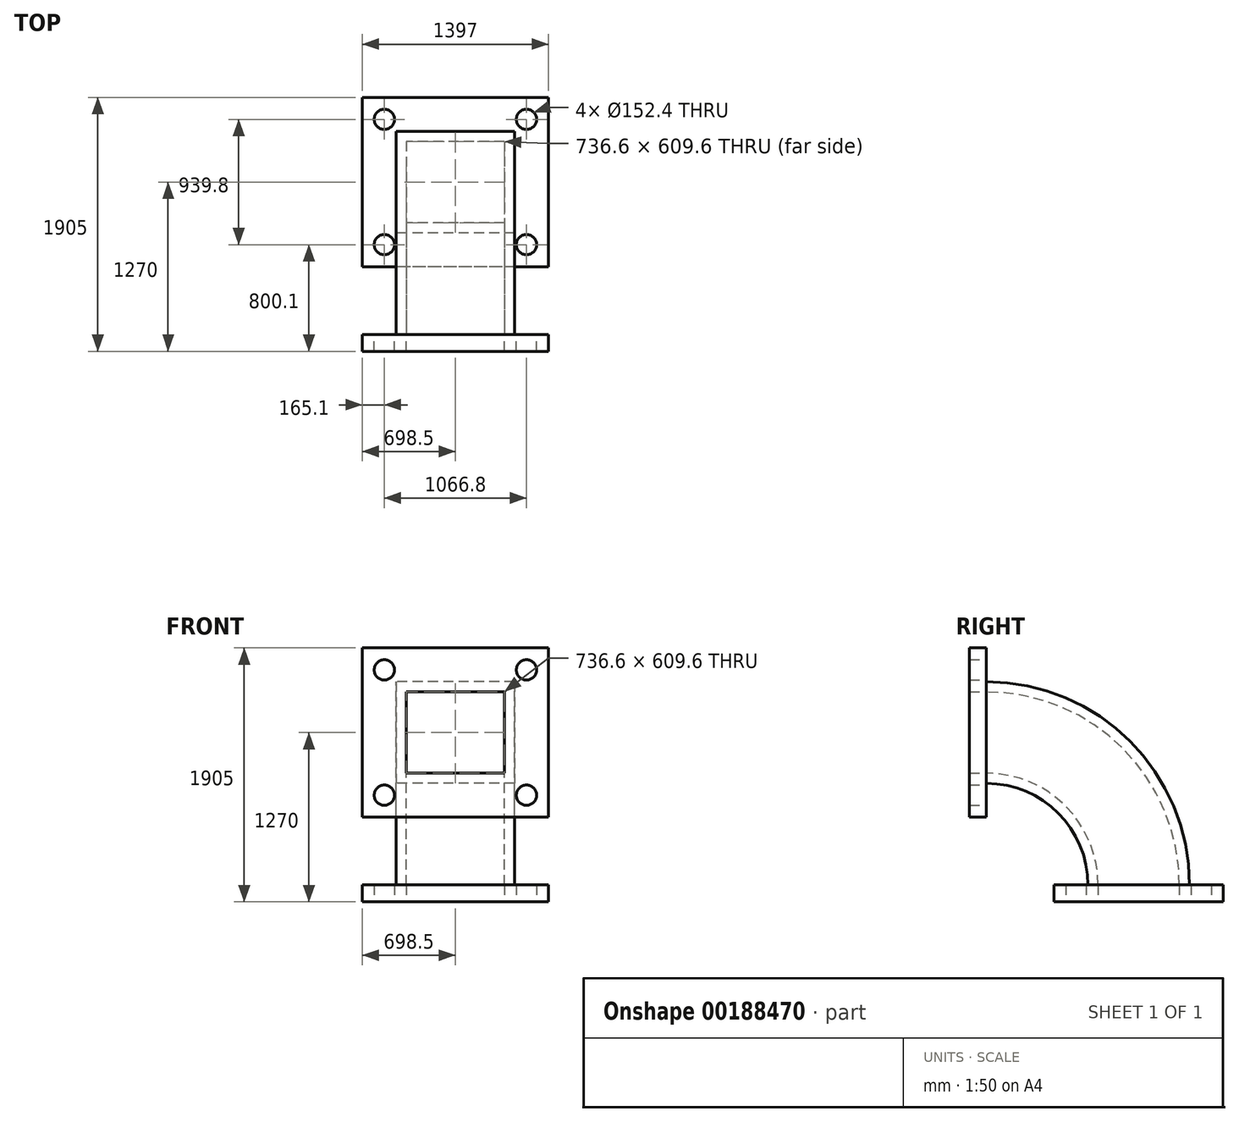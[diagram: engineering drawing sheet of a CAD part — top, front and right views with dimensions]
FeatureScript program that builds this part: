
annotation { "Feature Type Name" : "Feature", "Feature Type Description" : "" }
export const myFeature = defineFeature(function(context is Context, id is Id, definition is map)
    precondition{}
    {
        {
            var Q0;
            Q0=qCreatedBy(makeId("Front.planeOp"),FACE);
            var sketch = newSketch(context, id + "F0", { "sketchPlane" : qUnion([Q0])});
            skLineSegment(sketch, "E0.bottom", {"start": v(698.5, 635) * mm, "end": v(-698.5, 635) * mm});
            skLineSegment(sketch, "E0.top", {"start": v(698.5, -635) * mm, "end": v(-698.5, -635) * mm});
            skLineSegment(sketch, "E0.left", {"start": v(698.5, 635) * mm, "end": v(698.5, -635) * mm});
            skLineSegment(sketch, "E0.right", {"start": v(-698.5, 635) * mm, "end": v(-698.5, -635) * mm});
            skPoint(sketch, "E0.middle", {"position": v(0, 0) * mm});
            skLineSegment(sketch, "E1.bottom", {"start": v(368.3, 304.8) * mm, "end": v(-368.3, 304.8) * mm});
            skLineSegment(sketch, "E1.top", {"start": v(368.3, -304.8) * mm, "end": v(-368.3, -304.8) * mm});
            skLineSegment(sketch, "E1.left", {"start": v(368.3, 304.8) * mm, "end": v(368.3, -304.8) * mm});
            skLineSegment(sketch, "E1.right", {"start": v(-368.3, 304.8) * mm, "end": v(-368.3, -304.8) * mm});
            skCircle(sketch, "E2", {"center": v(533.4, 469.9) * mm, "radius": 76.2 * mm});
            skPoint(sketch, "E3.startSnap0", {"position": v(-698.5, 0) * mm});
            skCircle(sketch, "E4.MirrorC", {"center": v(-533.4, 469.9) * mm, "radius": 76.2 * mm});
            skCircle(sketch, "E5.MirrorC", {"center": v(-533.4, -469.9) * mm, "radius": 76.2 * mm});
            skCircle(sketch, "E6.MirrorC", {"center": v(533.4, -469.9) * mm, "radius": 76.2 * mm});
            skSolve(sketch);
        }
        {
            var Q0;
            Q0=qCreatedBy(makeId("Right.planeOp"),FACE);
            var sketch = newSketch(context, id + "F1", { "sketchPlane" : qUnion([Q0])});
            skCircle(sketch, "E7", {"center": v(0, -1143) * mm, "radius": 838.2 * mm});
            skCircle(sketch, "E8", {"center": v(0, -1143) * mm, "radius": 762 * mm});
            skLineSegment(sketch, "E9", {"start": v(-678.7, -1143) * mm, "end": v(1388.13, -1143) * mm});
            skSolve(sketch);
        }
        {
            var Q0;
            Q0=makeQuery(id+"F0.imprint","IMPRINT",FACE,{"disambiguationData":[TD([[makeQuery(id+"F0.imprint","IMPRINT",EDGE,{"derivedFrom":sQuery(id+"F0.wireOp",EDGE,"E0.bottom")}),1.0]])]});
            extrude(context, id + "F2", {"entities" : qUnion([Q0]), "depth" : 127 * mm});
        }
        {
            var Q0;
            Q0=makeQuery(id+"F2.opExtrude","CAP_FACE",FACE,{"disambiguationData":[OSD([sQuery(id+"F0.wireOp",EDGE,"E0.bottom"),sQuery(id+"F0.wireOp",EDGE,"E0.top"),sQuery(id+"F0.wireOp",EDGE,"E0.left"),sQuery(id+"F0.wireOp",EDGE,"E0.right"),sQuery(id+"F0.wireOp",EDGE,"E1.bottom"),sQuery(id+"F0.wireOp",EDGE,"E1.top"),sQuery(id+"F0.wireOp",EDGE,"E1.left"),sQuery(id+"F0.wireOp",EDGE,"E1.right"),sQuery(id+"F0.wireOp",EDGE,"E2"),sQuery(id+"F0.wireOp",EDGE,"E4.MirrorC"),sQuery(id+"F0.wireOp",EDGE,"E5.MirrorC"),sQuery(id+"F0.wireOp",EDGE,"E6.MirrorC")])],"isStart":true});
            var sketch = newSketch(context, id + "F3", { "sketchPlane" : qUnion([Q0])});
            skLineSegment(sketch, "E10.bottom", {"start": v(-444.5, 381) * mm, "end": v(444.5, 381) * mm});
            skLineSegment(sketch, "E10.top", {"start": v(-444.5, -381) * mm, "end": v(444.5, -381) * mm});
            skLineSegment(sketch, "E10.left", {"start": v(-444.5, 381) * mm, "end": v(-444.5, -381) * mm});
            skLineSegment(sketch, "E10.right", {"start": v(444.5, 381) * mm, "end": v(444.5, -381) * mm});
            skPoint(sketch, "E10.middle", {"position": v(0, 0) * mm});
            skSolve(sketch);
        }
        {
            var Q0;
            Q0=qCreatedBy(makeId("Top.planeOp"),FACE);
            var Q1;
            Q1=sQuery(id+"F1.wireOp",VERTEX,"E8.center");
            cPlane(context, id + "F4", {"entities" : qUnion([Q0, Q1]), "cplaneType" : CPlaneType.PLANE_POINT, "offset" : 25.4 * mm, "width" : 152.4 * mm, "height" : 152.4 * mm});
        }
        {
            var Q0;
            Q0=qCreatedBy(id+"F4.planeOp",FACE);
            var sketch = newSketch(context, id + "F5", { "sketchPlane" : qUnion([Q0])});
            skLineSegment(sketch, "E11", {"start": v(0, -161.15) * mm, "end": v(0, 243.03) * mm});
            skLineSegment(sketch, "E12", {"start": v(-90.84, 0) * mm, "end": v(129.22, 0) * mm});
            skSolve(sketch);
        }
        {
            var Q0;
            Q0=makeQuery(id+"F3.imprint","IMPRINT",FACE,{"disambiguationData":[TD([[makeQuery(id+"F3.imprint","IMPRINT",EDGE,{"derivedFrom":sQuery(id+"F3.wireOp",EDGE,"E10.bottom")}),-1.0]])]});
            var Q1;
            Q1=sQuery(id+"F5.wireOp",EDGE,"E12");
            revolve(context, id + "F6", {"entities" : qUnion([Q0]), "axis" : qUnion([Q1]), "revolveType" : RevolveType.ONE_DIRECTION, "oppositeDirection" : true, "angle" : 90 * degree});
        }
        {
            var Q0;
            Q0=makeQuery(id+"F2.opExtrude","SWEPT_BODY",BODY,{"disambiguationData":[OSD([sQuery(id+"F0.wireOp",EDGE,"E0.bottom"),sQuery(id+"F0.wireOp",EDGE,"E0.top"),sQuery(id+"F0.wireOp",EDGE,"E0.left"),sQuery(id+"F0.wireOp",EDGE,"E0.right"),sQuery(id+"F0.wireOp",EDGE,"E1.bottom"),sQuery(id+"F0.wireOp",EDGE,"E1.top"),sQuery(id+"F0.wireOp",EDGE,"E1.left"),sQuery(id+"F0.wireOp",EDGE,"E1.right"),sQuery(id+"F0.wireOp",EDGE,"E2"),sQuery(id+"F0.wireOp",EDGE,"E4.MirrorC"),sQuery(id+"F0.wireOp",EDGE,"E5.MirrorC"),sQuery(id+"F0.wireOp",EDGE,"E6.MirrorC")])]});
            var Q1;
            Q1=makeQuery(id+"F2.opExtrude","CAP_VERTEX",VERTEX,{"disambiguationData":[OSD([sQuery(id+"F0.wireOp",EDGE,"E0.top"),sQuery(id+"F0.wireOp",EDGE,"E0.left")])],"isStart":false});
            var Q2;
            Q2=makeQuery(id+"F2.opExtrude","CAP_VERTEX",VERTEX,{"disambiguationData":[OSD([sQuery(id+"F0.wireOp",EDGE,"E0.top"),sQuery(id+"F0.wireOp",EDGE,"E0.left")])],"isStart":true});
            transform(context, id + "F7", {"entities" : qUnion([Q0]), "transformType" : TransformType.TRANSLATION_ENTITY, "oppositeDirectionEntity" : false, "transformLine" : qUnion([Q1, Q2]), "makeCopy" : true});
        }
        {
            var Q0;
            Q0=makeQuery(id+"F7.opPattern","COPY",BODY,{"derivedFrom":makeQuery(id+"F2.opExtrude","SWEPT_BODY",BODY,{"disambiguationData":[OSD([sQuery(id+"F0.wireOp",EDGE,"E0.bottom"),sQuery(id+"F0.wireOp",EDGE,"E0.top"),sQuery(id+"F0.wireOp",EDGE,"E0.left"),sQuery(id+"F0.wireOp",EDGE,"E0.right"),sQuery(id+"F0.wireOp",EDGE,"E1.bottom"),sQuery(id+"F0.wireOp",EDGE,"E1.top"),sQuery(id+"F0.wireOp",EDGE,"E1.left"),sQuery(id+"F0.wireOp",EDGE,"E1.right"),sQuery(id+"F0.wireOp",EDGE,"E2"),sQuery(id+"F0.wireOp",EDGE,"E4.MirrorC"),sQuery(id+"F0.wireOp",EDGE,"E5.MirrorC"),sQuery(id+"F0.wireOp",EDGE,"E6.MirrorC")])]}),"instanceName":"1"});
            var Q1;
            Q1=sQuery(id+"F5.wireOp",EDGE,"E12");
            transform(context, id + "F8", {"entities" : qUnion([Q0]), "transformType" : TransformType.ROTATION, "transformAxis" : qUnion([Q1]), "angle" : 90 * degree, "oppositeDirection" : true, "makeCopy" : false});
        }
    });
